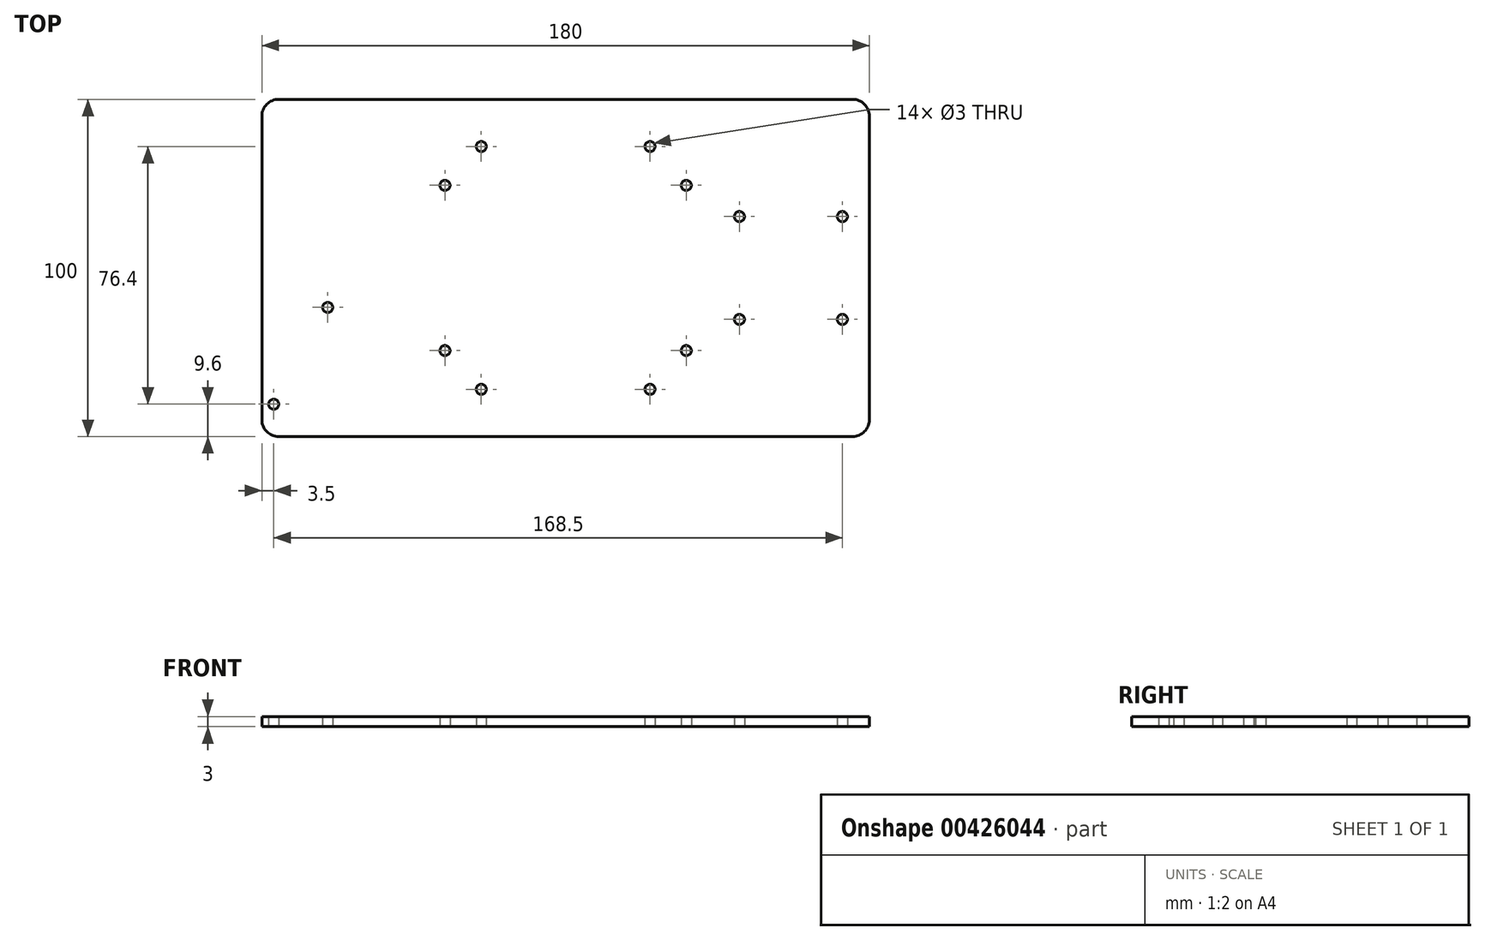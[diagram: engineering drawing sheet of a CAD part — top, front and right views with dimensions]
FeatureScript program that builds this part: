
annotation { "Feature Type Name" : "Feature", "Feature Type Description" : "" }
export const myFeature = defineFeature(function(context is Context, id is Id, definition is map)
    precondition{}
    {
        {
            var Q0;
            Q0=qCreatedBy(makeId("Top.planeOp"),FACE);
            var sketch = newSketch(context, id + "F0", { "sketchPlane" : qUnion([Q0])});
            skLineSegment(sketch, "E0.bottom", {"start": v(85, -50) * mm, "end": v(-85, -50) * mm});
            skLineSegment(sketch, "E0.top", {"start": v(85, 50) * mm, "end": v(-85, 50) * mm});
            skLineSegment(sketch, "E0.left", {"start": v(90, -45) * mm, "end": v(90, 45) * mm});
            skLineSegment(sketch, "E0.right", {"start": v(-90, -45) * mm, "end": v(-90, 45) * mm});
            skPoint(sketch, "E0.middle", {"position": v(0, 0) * mm});
            skCircle(sketch, "E1", {"center": v(-35.75, 24.5) * mm, "radius": 1.5 * mm});
            skCircle(sketch, "E2.MirrorC", {"center": v(35.75, 24.5) * mm, "radius": 1.5 * mm});
            skCircle(sketch, "E3.MirrorC", {"center": v(-35.75, -24.5) * mm, "radius": 1.5 * mm});
            skCircle(sketch, "E4.MirrorC", {"center": v(35.75, -24.5) * mm, "radius": 1.5 * mm});
            skCircle(sketch, "E5", {"center": v(-25, -36) * mm, "radius": 1.5 * mm});
            skCircle(sketch, "E6.MirrorC", {"center": v(25, -36) * mm, "radius": 1.5 * mm});
            skCircle(sketch, "E7.MirrorC", {"center": v(-25, 36) * mm, "radius": 1.5 * mm});
            skCircle(sketch, "E8.MirrorC", {"center": v(25, 36) * mm, "radius": 1.5 * mm});
            skCircle(sketch, "E9", {"center": v(82, 15.25) * mm, "radius": 1.5 * mm});
            skCircle(sketch, "E10.MirrorC", {"center": v(82, -15.25) * mm, "radius": 1.5 * mm});
            skLineSegment(sketch, "E11", {"start": v(66.75, 50) * mm, "end": v(66.75, -50) * mm, "construction": true});
            skCircle(sketch, "E12.MirrorC", {"center": v(51.5, 15.25) * mm, "radius": 1.5 * mm});
            skCircle(sketch, "E13.MirrorC", {"center": v(51.5, -15.25) * mm, "radius": 1.5 * mm});
            skCircle(sketch, "E14.MirrorC", {"center": v(-86.5, -40.4) * mm, "radius": 1.5 * mm});
            skCircle(sketch, "E15.MirrorC", {"center": v(-70.5, -11.7) * mm, "radius": 1.5 * mm});
            skPoint(sketch, "E16.visualSharp", {"position": v(-90, 50) * mm});
            skArc(sketch, "E16.filletArc", {"start": v(-85, 50) * mm, "mid": v(-88.54, 48.54) * mm, "end": v(-90, 45) * mm});
            skPoint(sketch, "E17.visualSharp", {"position": v(-90, -50) * mm});
            skArc(sketch, "E17.filletArc", {"start": v(-90, -45) * mm, "mid": v(-88.54, -48.54) * mm, "end": v(-85, -50) * mm});
            skPoint(sketch, "E18.visualSharp", {"position": v(90, -50) * mm});
            skArc(sketch, "E18.filletArc", {"start": v(85, -50) * mm, "mid": v(88.54, -48.54) * mm, "end": v(90, -45) * mm});
            skPoint(sketch, "E19.visualSharp", {"position": v(90, 50) * mm});
            skArc(sketch, "E19.filletArc", {"start": v(90, 45) * mm, "mid": v(88.54, 48.54) * mm, "end": v(85, 50) * mm});
            skSolve(sketch);
        }
        {
            var Q0;
            Q0=makeQuery(id+"F0.imprint","IMPRINT",FACE,{"disambiguationData":[TD([[makeQuery(id+"F0.imprint","IMPRINT",EDGE,{"derivedFrom":sQuery(id+"F0.wireOp",EDGE,"E0.bottom")}),-1.0]])]});
            extrude(context, id + "F1", {"entities" : qUnion([Q0]), "depth" : 3 * mm});
        }
    });
